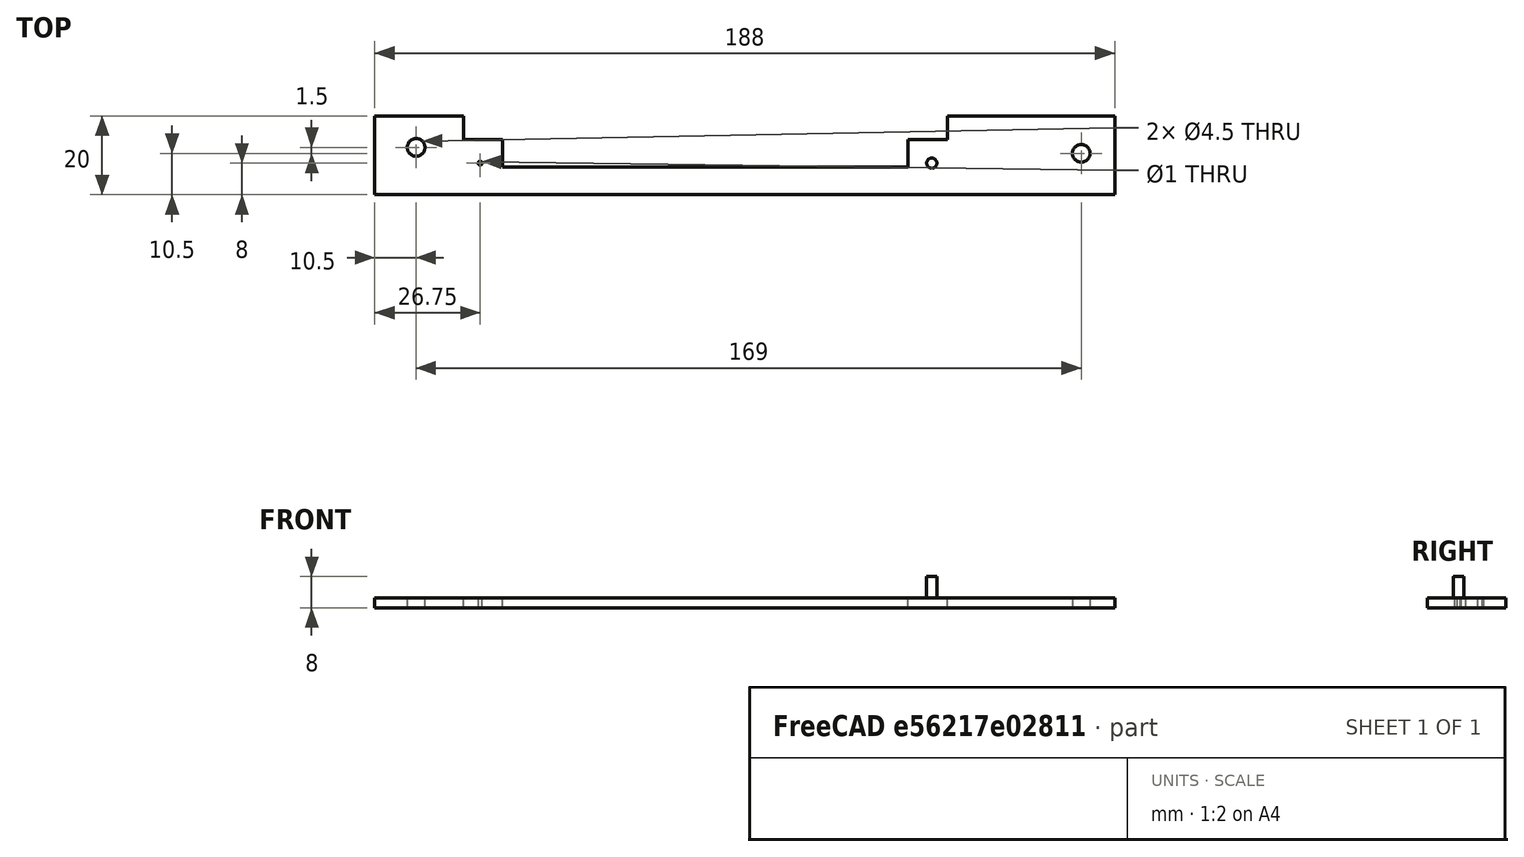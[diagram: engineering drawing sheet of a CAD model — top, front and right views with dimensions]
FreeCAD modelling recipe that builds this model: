
FCSTD DOCUMENT  (FreeCAD 0.21R33668 +26 (Git))
Label: 3-vector-support-rt
License: All rights reserved
LicenseURL: http://en.wikipedia.org/wiki/All_rights_reserved
objects: PartDesign::SubtractiveCylinder×3, PartDesign::SubtractiveBox×2, PartDesign::AdditiveBox×1, PartDesign::AdditiveCylinder×1, PartDesign::Body×1
note: 15 computed .brp shape members not serialized (recipe doc carries the construction recipe); baked Part::Feature solids carry a one-line shape summary decoded from their .brp

FEATURE [PartDesign::AdditiveBox] Box  label="bar-1"
  AttacherType = Attacher::AttachEngine3D
  Height = 2.5
  Length = 188
  Width = 20
FEATURE [PartDesign::SubtractiveCylinder] Cylinder  label="mp1"
  Angle = 360
  AttacherType = Attacher::AttachEngine3D
  AttachmentOffset = pos=(10.5,12,-2.5) rot=(0,0,1;0rad)
  BaseFeature = -> Box
  FirstAngle = 0
  Height = 2.5
  MapMode = 5
  Placement = pos=(10.5,12,0) rot=(0,0,1;0rad)
  Radius = 2.25
  SecondAngle = 0
  Support = -> [Box]
FEATURE [PartDesign::SubtractiveCylinder] Cylinder001  label="mp2"
  Angle = 360
  AttacherType = Attacher::AttachEngine3D
  AttachmentOffset = pos=(169,-1.5,-2.5) rot=(0,0,1;0rad)
  BaseFeature = -> Cylinder
  FirstAngle = 0
  Height = 2.5
  MapMode = 5
  Placement = pos=(179.5,10.5,0) rot=(0,0,1;0rad)
  Radius = 2.25
  SecondAngle = 0
  Support = -> [Cylinder]
FEATURE [PartDesign::SubtractiveBox] Box001  label="negative-1"
  AttacherType = Attacher::AttachEngine3D
  AttachmentOffset = pos=(-157,3.5,0) rot=(0,0,1;0rad)
  BaseFeature = -> Cylinder001
  Height = 2.5
  Length = 123
  MapMode = 2
  Placement = pos=(22.5,14,0) rot=(0,0,1;0rad)
  Support = -> [Cylinder001]
  Width = 6
FEATURE [PartDesign::SubtractiveBox] Box002  label="negative-2"
  AttacherType = Attacher::AttachEngine3D
  AttachmentOffset = pos=(-147,-3.5,0) rot=(0,0,1;0rad)
  BaseFeature = -> Box001
  Height = 2.5
  Length = 103
  MapMode = 2
  Placement = pos=(32.5,7,0) rot=(0,0,1;0rad)
  Support = -> [Cylinder001]
  Width = 7
FEATURE [PartDesign::AdditiveCylinder] Cylinder003  label="mount-lg"
  Angle = 360
  AttacherType = Attacher::AttachEngine3D
  AttachmentOffset = pos=(109,1,2) rot=(0,0,1;0rad)
  BaseFeature = -> Box002
  FirstAngle = 0
  Height = 6
  MapMode = 2
  Placement = pos=(141.5,8,2) rot=(0,0,1;0rad)
  Radius = 1.3
  SecondAngle = 0
  Support = -> [Box002]
FEATURE [PartDesign::SubtractiveCylinder] Cylinder004  label="mount-neg"
  Angle = 360
  AttacherType = Attacher::AttachEngine3D
  AttachmentOffset = pos=(-114.75,0,-2.5) rot=(0,0,1;0rad)
  BaseFeature = -> Cylinder003
  FirstAngle = 0
  Height = 2.5
  MapMode = 5
  Placement = pos=(26.75,8,0) rot=(0,0,1;0rad)
  Radius = 0.5
  SecondAngle = 0
  Support = -> [Cylinder003]
FEATURE [PartDesign::Body] Body  label="Mount-right"
  Group = -> [Box,Cylinder,Cylinder001,Box001,Box002,Cylinder003,Cylinder004]
  Origin = -> Origin
  Tip = -> Cylinder004
